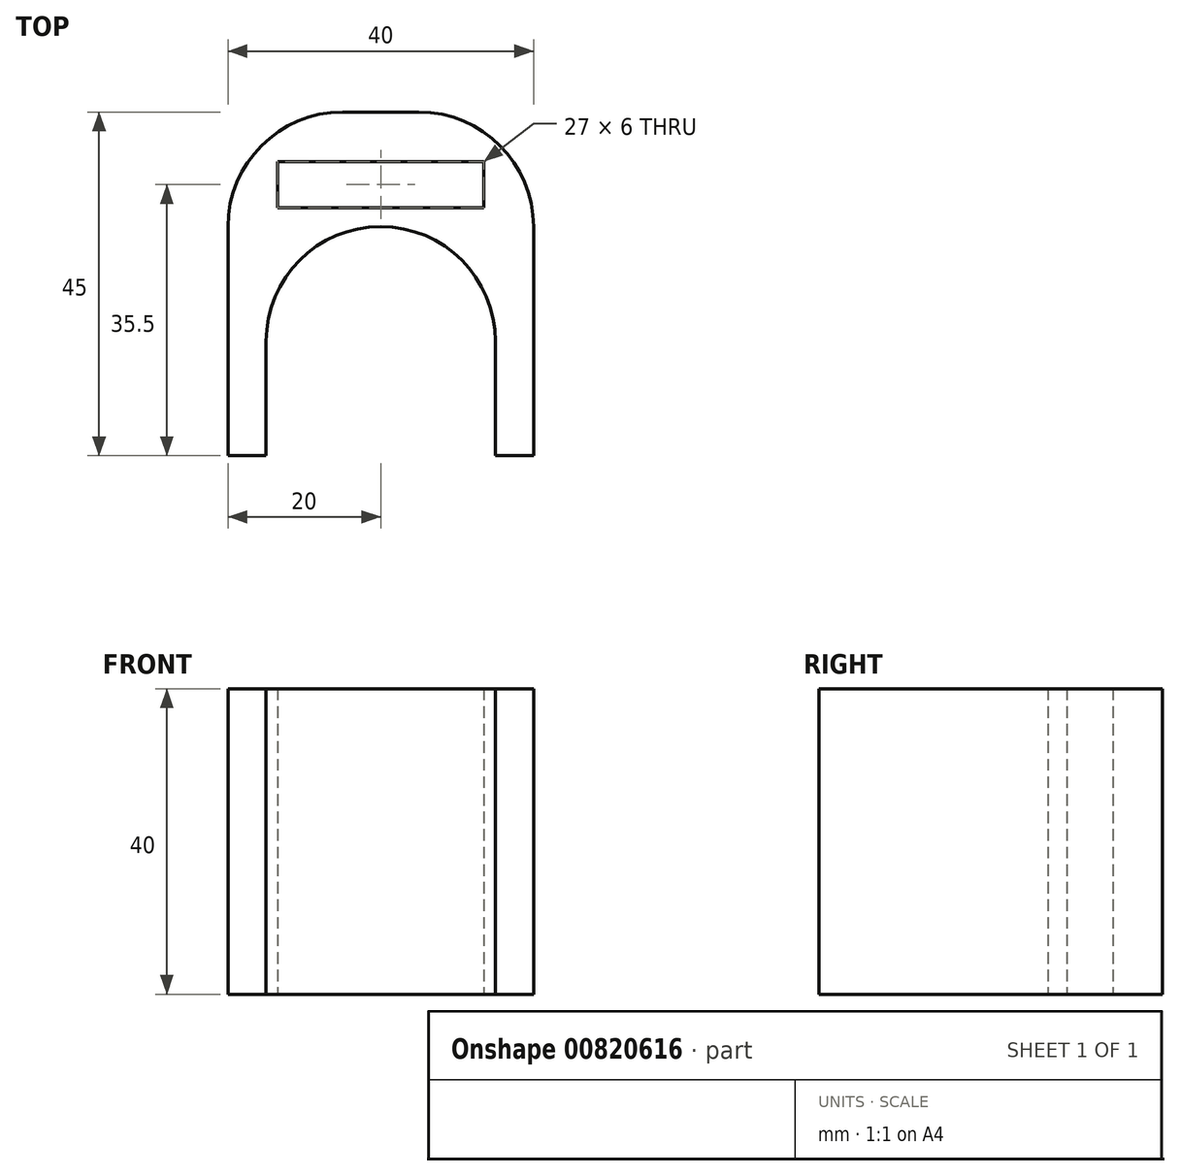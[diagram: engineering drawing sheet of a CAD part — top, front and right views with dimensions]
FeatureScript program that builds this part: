
annotation { "Feature Type Name" : "Feature", "Feature Type Description" : "" }
export const myFeature = defineFeature(function(context is Context, id is Id, definition is map)
    precondition{}
    {
        {
            var Q0;
            Q0=qCreatedBy(makeId("Top.planeOp"),FACE);
            var sketch = newSketch(context, id + "F0", { "sketchPlane" : qUnion([Q0])});
            skLineSegment(sketch, "E0", {"start": v(0, 0) * mm, "end": v(5, 0) * mm});
            skLineSegment(sketch, "E1", {"start": v(0, 0) * mm, "end": v(0, 30) * mm});
            skLineSegment(sketch, "E2", {"start": v(5, 0) * mm, "end": v(5, 15) * mm});
            skLineSegment(sketch, "E3", {"start": v(5, 0) * mm, "end": v(35, 0) * mm, "construction": true});
            skLineSegment(sketch, "E4", {"start": v(35, 0) * mm, "end": v(40, 0) * mm});
            skLineSegment(sketch, "E5", {"start": v(40, 0) * mm, "end": v(40, 30) * mm});
            skLineSegment(sketch, "E6", {"start": v(35, 0) * mm, "end": v(35, 15) * mm});
            skLineSegment(sketch, "E7", {"start": v(20, 30) * mm, "end": v(20, 30) * mm});
            skPoint(sketch, "E8.visualSharp", {"position": v(5, 30) * mm});
            skArc(sketch, "E8.filletArc", {"start": v(20, 30) * mm, "mid": v(9.4, 25.6) * mm, "end": v(5, 15) * mm});
            skPoint(sketch, "E9.visualSharp", {"position": v(35, 30) * mm});
            skArc(sketch, "E9.filletArc", {"start": v(35, 15) * mm, "mid": v(30.6, 25.6) * mm, "end": v(20, 30) * mm});
            skLineSegment(sketch, "E10", {"start": v(0, 30) * mm, "end": v(0, 30) * mm});
            skLineSegment(sketch, "E11", {"start": v(40, 30) * mm, "end": v(40, 30) * mm});
            skLineSegment(sketch, "E12", {"start": v(25, 45) * mm, "end": v(15, 45) * mm});
            skPoint(sketch, "E13.visualSharp", {"position": v(0, 45) * mm});
            skArc(sketch, "E13.filletArc", {"start": v(15, 45) * mm, "mid": v(4.4, 40.6) * mm, "end": v(0, 30) * mm});
            skPoint(sketch, "E14.visualSharp", {"position": v(40, 45) * mm});
            skArc(sketch, "E14.filletArc", {"start": v(40, 30) * mm, "mid": v(35.6, 40.6) * mm, "end": v(25, 45) * mm});
            skPoint(sketch, "E15.middle", {"position": v(18.5, 27.5) * mm});
            skLineSegment(sketch, "E16", {"start": v(20, 30) * mm, "end": v(20, 35.5) * mm, "construction": true});
            skLineSegment(sketch, "E17.bottom", {"start": v(33.5, 32.5) * mm, "end": v(6.5, 32.5) * mm});
            skLineSegment(sketch, "E17.top", {"start": v(33.5, 38.5) * mm, "end": v(6.5, 38.5) * mm});
            skLineSegment(sketch, "E17.left", {"start": v(33.5, 32.5) * mm, "end": v(33.5, 38.5) * mm});
            skLineSegment(sketch, "E17.right", {"start": v(6.5, 32.5) * mm, "end": v(6.5, 38.5) * mm});
            skPoint(sketch, "E17.middle", {"position": v(20, 35.5) * mm});
            skSolve(sketch);
        }
        {
            var Q0;
            Q0=qSketchRegion(id+"F0",true);
            extrude(context, id + "F1", {"entities" : qUnion([Q0]), "depth" : 40 * mm, "offsetDistance" : 25 * mm});
        }
    });
